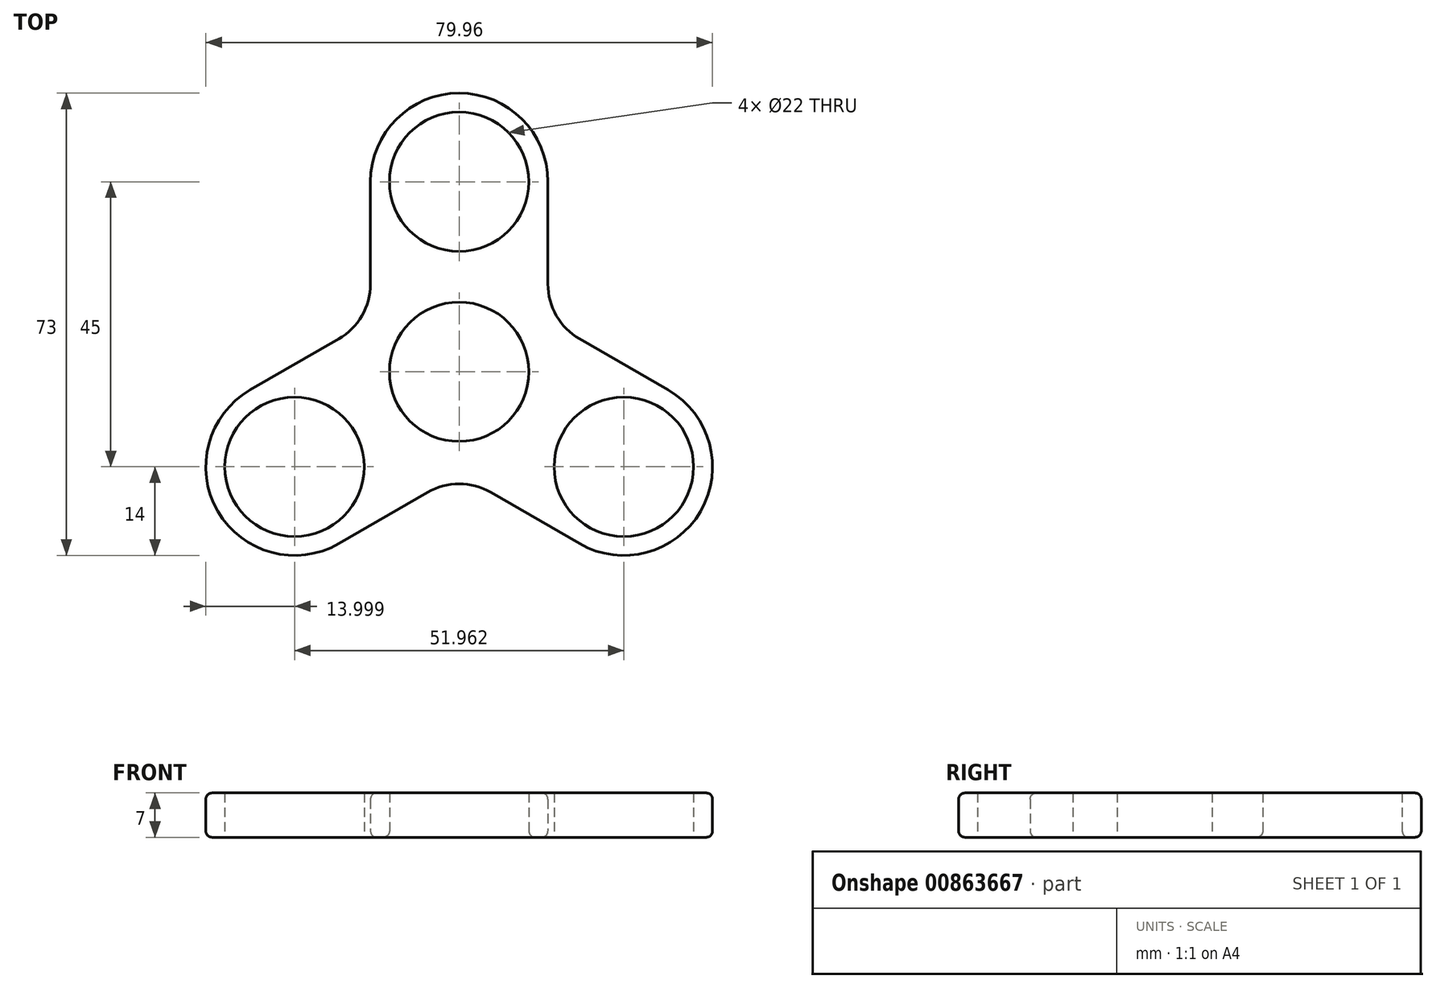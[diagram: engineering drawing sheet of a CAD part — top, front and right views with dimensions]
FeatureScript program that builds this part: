
annotation { "Feature Type Name" : "Feature", "Feature Type Description" : "" }
export const myFeature = defineFeature(function(context is Context, id is Id, definition is map)
    precondition{}
    {
        {
            var Q0;
            Q0=qCreatedBy(makeId("Top.planeOp"),FACE);
            var sketch = newSketch(context, id + "F0", { "sketchPlane" : qUnion([Q0])});
            skCircle(sketch, "E0", {"center": v(0, 0) * mm, "radius": 11 * mm});
            skCircle(sketch, "E1", {"center": v(0, 30) * mm, "radius": 11 * mm});
            skCircle(sketch, "E2.1.0", {"center": v(25.98, -15) * mm, "radius": 11 * mm});
            skCircle(sketch, "E2.2.0", {"center": v(-25.98, -15) * mm, "radius": 11 * mm});
            skLineSegment(sketch, "E2.anchor1", {"start": v(0, 0) * mm, "end": v(0, 30) * mm, "construction": true});
            skLineSegment(sketch, "E2.anchor2", {"start": v(0, 0) * mm, "end": v(-25.98, -15) * mm, "construction": true});
            skArc(sketch, "E3", {"start": v(-18.98, -27.12) * mm, "mid": v(-38.1, -22) * mm, "end": v(-32.98, -2.88) * mm});
            skLineSegment(sketch, "E4", {"start": v(-18.98, -27.12) * mm, "end": v(-5, -19.05) * mm});
            skLineSegment(sketch, "E5", {"start": v(-32.98, -2.88) * mm, "end": v(-19, 5.2) * mm});
            skLineSegment(sketch, "E6.1.0", {"start": v(18.98, -27.12) * mm, "end": v(5, -19.05) * mm});
            skArc(sketch, "E6.1.1", {"start": v(32.98, -2.88) * mm, "mid": v(38.1, -22) * mm, "end": v(18.98, -27.12) * mm});
            skLineSegment(sketch, "E6.1.2", {"start": v(32.98, -2.88) * mm, "end": v(19, 5.2) * mm});
            skLineSegment(sketch, "E6.2.0", {"start": v(14, 30) * mm, "end": v(14, 13.86) * mm});
            skArc(sketch, "E6.2.1", {"start": v(-14, 30) * mm, "mid": v(0, 44) * mm, "end": v(14, 30) * mm});
            skLineSegment(sketch, "E6.2.2", {"start": v(-14, 30) * mm, "end": v(-14, 13.86) * mm});
            skPoint(sketch, "E7.orphan", {"position": v(-14, -8.08) * mm});
            skPoint(sketch, "E8.orphan", {"position": v(14, -8.08) * mm});
            skPoint(sketch, "E9.orphan", {"position": v(0, 16.17) * mm});
            skPoint(sketch, "E10.visualSharp", {"position": v(-14, 8.08) * mm});
            skArc(sketch, "E10.filletArc", {"start": v(-19, 5.2) * mm, "mid": v(-15.34, 8.86) * mm, "end": v(-14, 13.86) * mm});
            skPoint(sketch, "E11.visualSharp", {"position": v(14, 8.08) * mm});
            skArc(sketch, "E11.filletArc", {"start": v(14, 13.86) * mm, "mid": v(15.34, 8.86) * mm, "end": v(19, 5.2) * mm});
            skPoint(sketch, "E12.visualSharp", {"position": v(0, -16.17) * mm});
            skArc(sketch, "E12.filletArc", {"start": v(5, -19.05) * mm, "mid": v(0, -17.71) * mm, "end": v(-5, -19.05) * mm});
            skSolve(sketch);
        }
        {
            var Q0;
            Q0 = qSketchRegion(id + "F0", true);
            extrude(context, id + "F1", {"entities" : qUnion([Q0]), "endBound" : BoundingType.SYMMETRIC, "depth" : 7 * mm, "offsetDistance" : 25 * mm});
        }
        {
            var Q0;
            Q0=makeQuery(id+"F1.opExtrude","CAP_EDGE",EDGE,{"disambiguationData":[OSD([sQuery(id+"F0.wireOp",EDGE,"E6.2.1")])],"isStart":false});
            var Q1;
            Q1=makeQuery(id+"F1.opExtrude","CAP_EDGE",EDGE,{"disambiguationData":[OSD([sQuery(id+"F0.wireOp",EDGE,"E6.2.0")])],"isStart":false});
            var Q2;
            Q2=makeQuery(id+"F1.opExtrude","CAP_EDGE",EDGE,{"disambiguationData":[OSD([sQuery(id+"F0.wireOp",EDGE,"E11.filletArc")])],"isStart":false});
            var Q3;
            Q3=makeQuery(id+"F1.opExtrude","CAP_EDGE",EDGE,{"disambiguationData":[OSD([sQuery(id+"F0.wireOp",EDGE,"E6.1.2")])],"isStart":false});
            var Q4;
            Q4=makeQuery(id+"F1.opExtrude","CAP_EDGE",EDGE,{"disambiguationData":[OSD([sQuery(id+"F0.wireOp",EDGE,"E6.1.1")])],"isStart":false});
            var Q5;
            Q5=makeQuery(id+"F1.opExtrude","CAP_EDGE",EDGE,{"disambiguationData":[OSD([sQuery(id+"F0.wireOp",EDGE,"E6.1.0")])],"isStart":false});
            var Q6;
            Q6=makeQuery(id+"F1.opExtrude","CAP_EDGE",EDGE,{"disambiguationData":[OSD([sQuery(id+"F0.wireOp",EDGE,"E12.filletArc")])],"isStart":false});
            var Q7;
            Q7=makeQuery(id+"F1.opExtrude","CAP_EDGE",EDGE,{"disambiguationData":[OSD([sQuery(id+"F0.wireOp",EDGE,"E4")])],"isStart":false});
            var Q8;
            Q8=makeQuery(id+"F1.opExtrude","CAP_EDGE",EDGE,{"disambiguationData":[OSD([sQuery(id+"F0.wireOp",EDGE,"E3")])],"isStart":false});
            var Q9;
            Q9=makeQuery(id+"F1.opExtrude","CAP_EDGE",EDGE,{"disambiguationData":[OSD([sQuery(id+"F0.wireOp",EDGE,"E5")])],"isStart":false});
            var Q10;
            Q10=makeQuery(id+"F1.opExtrude","CAP_EDGE",EDGE,{"disambiguationData":[OSD([sQuery(id+"F0.wireOp",EDGE,"E10.filletArc")])],"isStart":false});
            var Q11;
            Q11=makeQuery(id+"F1.opExtrude","CAP_EDGE",EDGE,{"disambiguationData":[OSD([sQuery(id+"F0.wireOp",EDGE,"E6.2.2")])],"isStart":false});
            fillet(context, id + "F2", {"entities" : qUnion([Q0, Q1, Q2, Q3, Q4, Q5, Q6, Q7, Q8, Q9, Q10, Q11]), "radius" : 1 * mm, "tangentPropagation" : true, "allowEdgeOverflow" : false});
        }
        {
            var Q0;
            Q0=makeQuery(id+"F1.opExtrude","CAP_EDGE",EDGE,{"disambiguationData":[OSD([sQuery(id+"F0.wireOp",EDGE,"E4")])],"isStart":true});
            var Q1;
            Q1=makeQuery(id+"F1.opExtrude","CAP_EDGE",EDGE,{"disambiguationData":[OSD([sQuery(id+"F0.wireOp",EDGE,"E3")])],"isStart":true});
            var Q2;
            Q2=makeQuery(id+"F1.opExtrude","CAP_EDGE",EDGE,{"disambiguationData":[OSD([sQuery(id+"F0.wireOp",EDGE,"E5")])],"isStart":true});
            var Q3;
            Q3=makeQuery(id+"F1.opExtrude","CAP_EDGE",EDGE,{"disambiguationData":[OSD([sQuery(id+"F0.wireOp",EDGE,"E10.filletArc")])],"isStart":true});
            var Q4;
            Q4=makeQuery(id+"F1.opExtrude","CAP_EDGE",EDGE,{"disambiguationData":[OSD([sQuery(id+"F0.wireOp",EDGE,"E6.2.2")])],"isStart":true});
            var Q5;
            Q5=makeQuery(id+"F1.opExtrude","CAP_EDGE",EDGE,{"disambiguationData":[OSD([sQuery(id+"F0.wireOp",EDGE,"E1")])],"isStart":true});
            var Q6;
            Q6=makeQuery(id+"F1.opExtrude","CAP_EDGE",EDGE,{"disambiguationData":[OSD([sQuery(id+"F0.wireOp",EDGE,"E6.2.0")])],"isStart":true});
            var Q7;
            Q7=makeQuery(id+"F1.opExtrude","CAP_EDGE",EDGE,{"disambiguationData":[OSD([sQuery(id+"F0.wireOp",EDGE,"E11.filletArc")])],"isStart":true});
            var Q8;
            Q8=makeQuery(id+"F1.opExtrude","CAP_EDGE",EDGE,{"disambiguationData":[OSD([sQuery(id+"F0.wireOp",EDGE,"E6.1.2")])],"isStart":true});
            var Q9;
            Q9=makeQuery(id+"F1.opExtrude","CAP_EDGE",EDGE,{"disambiguationData":[OSD([sQuery(id+"F0.wireOp",EDGE,"E6.1.1")])],"isStart":true});
            var Q10;
            Q10=makeQuery(id+"F1.opExtrude","CAP_EDGE",EDGE,{"disambiguationData":[OSD([sQuery(id+"F0.wireOp",EDGE,"E6.1.0")])],"isStart":true});
            var Q11;
            Q11=makeQuery(id+"F1.opExtrude","CAP_EDGE",EDGE,{"disambiguationData":[OSD([sQuery(id+"F0.wireOp",EDGE,"E12.filletArc")])],"isStart":true});
            fillet(context, id + "F3", {"entities" : qUnion([Q0, Q1, Q2, Q3, Q4, Q5, Q6, Q7, Q8, Q9, Q10, Q11]), "radius" : 1 * mm, "tangentPropagation" : true, "allowEdgeOverflow" : false});
        }
    });
